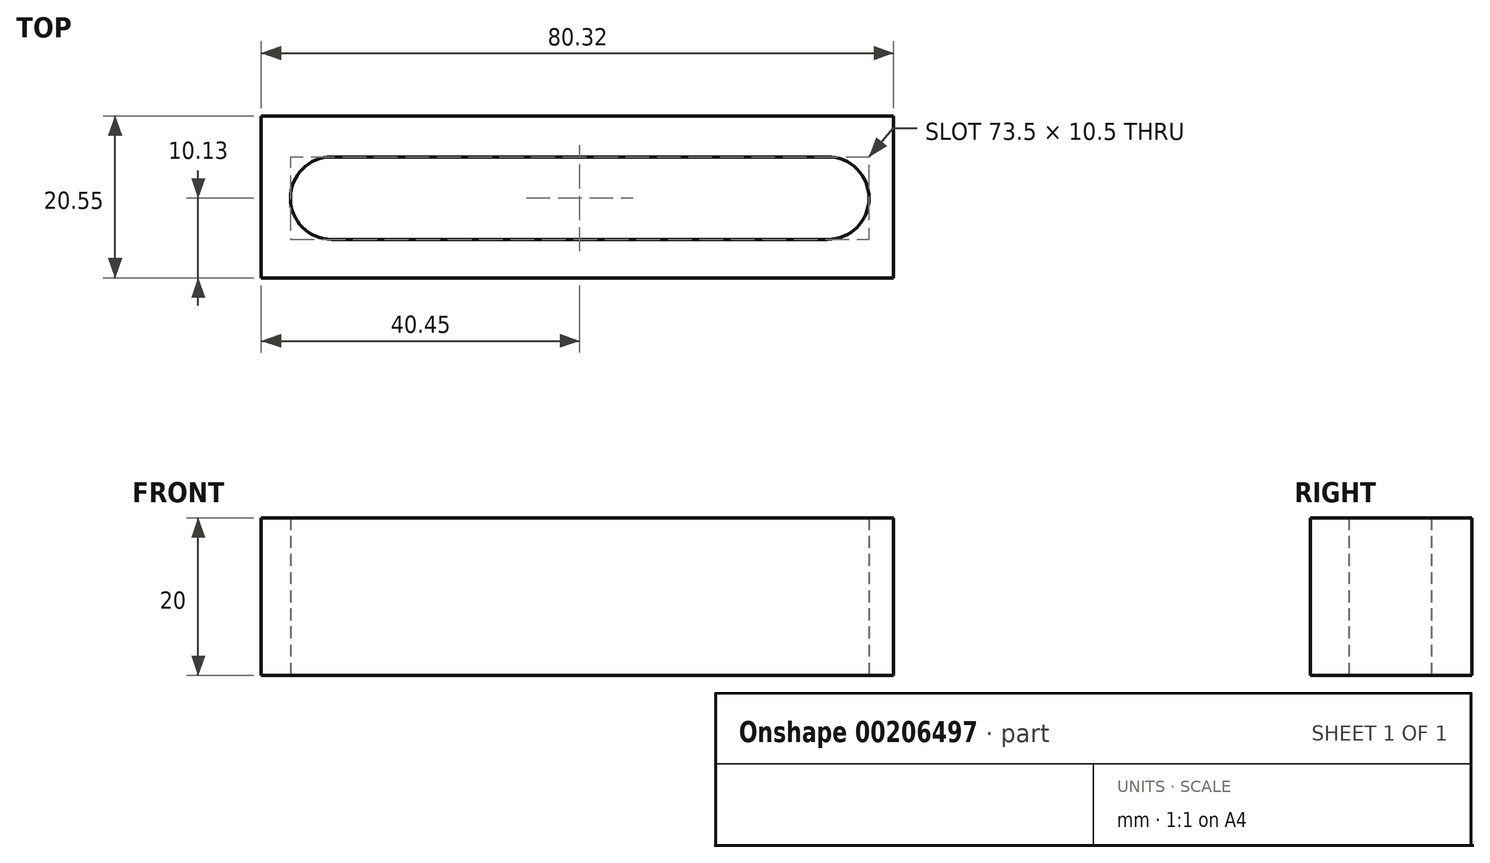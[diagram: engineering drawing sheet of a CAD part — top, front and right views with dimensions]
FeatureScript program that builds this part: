
annotation { "Feature Type Name" : "Feature", "Feature Type Description" : "" }
export const myFeature = defineFeature(function(context is Context, id is Id, definition is map)
    precondition{}
    {
        {
            var Q0;
            Q0=qCreatedBy(makeId("Top.planeOp"), FACE);
            var sketch = newSketch(context, id + "F0", { "sketchPlane" : qUnion([Q0])});
            skCircle(sketch, "E0", {"center": v(0, 0) * mm, "radius": 5.25 * mm});
            skCircle(sketch, "E1.1.0.0", {"center": v(10.5, 0) * mm, "radius": 5.25 * mm});
            skCircle(sketch, "E1.2.0.0", {"center": v(21, 0) * mm, "radius": 5.25 * mm});
            skCircle(sketch, "E1.3.0.0", {"center": v(31.5, 0) * mm, "radius": 5.25 * mm});
            skCircle(sketch, "E1.4.0.0", {"center": v(42, 0) * mm, "radius": 5.25 * mm});
            skCircle(sketch, "E1.5.0.0", {"center": v(52.5, 0) * mm, "radius": 5.25 * mm});
            skCircle(sketch, "E1.6.0.0", {"center": v(63, 0) * mm, "radius": 5.25 * mm});
            skLineSegment(sketch, "E1.direction1", {"start": v(0, 0) * mm, "end": v(10.5, 0) * mm, "construction": true});
            skLineSegment(sketch, "E2", {"start": v(0, 5.25) * mm, "end": v(63, 5.25) * mm});
            skLineSegment(sketch, "E3", {"start": v(0, -5.25) * mm, "end": v(63, -5.25) * mm});
            skLineSegment(sketch, "E4.bottom", {"start": v(-8.95, 10.42) * mm, "end": v(71.37, 10.42) * mm});
            skLineSegment(sketch, "E4.top", {"start": v(-8.95, -10.13) * mm, "end": v(71.37, -10.13) * mm});
            skLineSegment(sketch, "E4.left", {"start": v(-8.95, 10.42) * mm, "end": v(-8.95, -10.13) * mm});
            skLineSegment(sketch, "E4.right", {"start": v(71.37, 10.42) * mm, "end": v(71.37, -10.13) * mm});
            skSolve(sketch);
        }
        {
            var Q0;
            Q0 = qSketchRegion(id + "F0", true);
            extrude(context, id + "F1", {"entities" : qUnion([Q0]), "depth" : 20 * mm, "offsetDistance" : 25 * mm});
        }
    });
